# Revit family: Shower-Handshower-KOHLER-Rain_Duet-K-28016ME
name_source: partatom
category: Plumbing Fixtures
units: mm (PartAtom-declared; Revit-internal decimal feet)

## family parameters
Cut with Voids When Loaded = No
Host = Face
OmniClass Number = 23.31.17.00
OmniClass Title = Showers
Part Type = Normal
Room Calculation Point = No
Round Connector Dimension = Use Diameter
Shared = No

## types (4) — shared parameters
ADA Compliant = No
Assembly Code = D2010700
CW Connection = No
Cold Water Inlet = Cold Water Inlet
Date Modified = 01/31/2023
Default Elevation = 42"
Description = Multifunction Handshower Kit 120mm
Drain Included = No
Flow Rate = 0 GPM
HW Connection = Yes
Height = 27"
Hot Water Inlet = Hot Water Inlet
Length = 4 1/16"
Manufacturer = Kohler Co.
Master Format 2014 = 22 42 23
Master Format 2014 Name = Residential Showers
Material = Primum Metal Construction
Pressure = 0.00 psi
Product Documentation Link = https://me.kohler.com
Product Name = Rain Duet
Tempered Water Inlet = Tempered Water Inlet
Vent Connection = No
Waste Connection = No
Waste Water Outlet = Waste Water Outlet
WaterSense Certified = No
Width = 1 15/16"

## per-type parameters (varying)
| type | Finish | Model | Product Page URL | Type | URL |
| AF-Vibrant French Gold | Kohler-Metal-AF-Vibrant_French_Gold | K-28016ME-AF | https://me.kohler.com | 1 | https://www.us.kohler.com |
| BN-Vibrant Brushed Nickel | Kohler-Metal-BN-Vibrant_Brushed_Nickel | K-28016ME-BN |  | 2 | https://www.us.kohler.com |
| BV-Brushed Bronze | Kohler-Metal-BV-Brushed_Bronze | K-28016ME-BV | https://me.kohler.com | 3 | https://me.kohler.com |
| CP-Polished Chrome | Kohler-Metal-CP-Polished_Chrome | K-28016ME-CP | https://me.kohler.com | 4 | https://www.us.kohler.com |

## geometry (parser evidence)
native form markers: Sweep x5
no freeform markers — native parametric forms only
